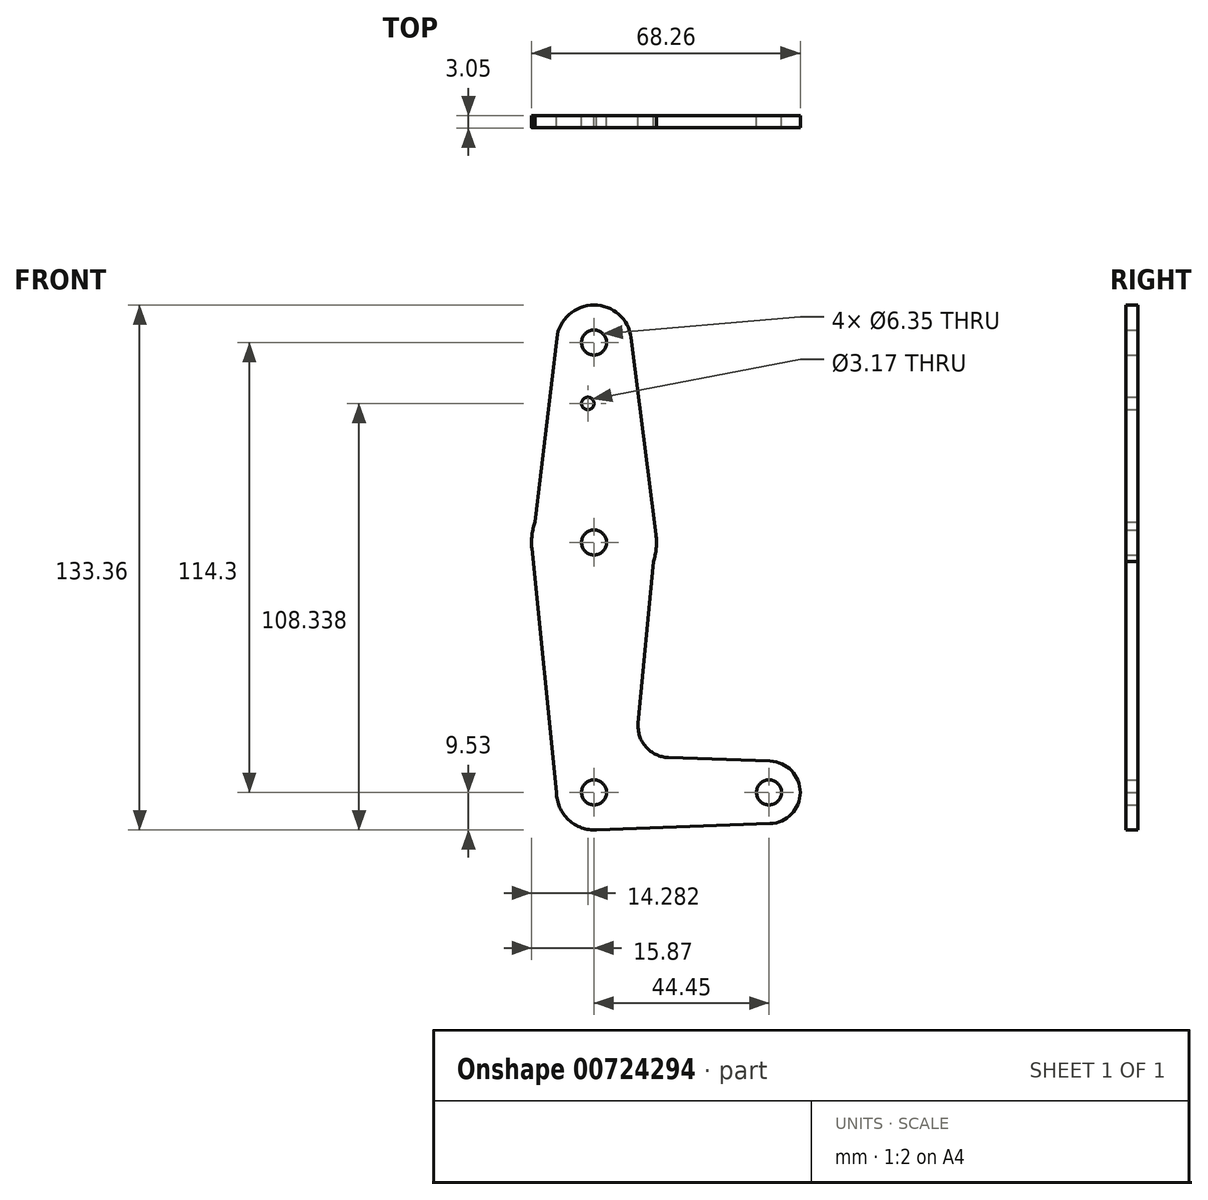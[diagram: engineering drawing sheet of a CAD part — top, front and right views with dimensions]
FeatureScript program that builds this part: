
annotation { "Feature Type Name" : "Feature", "Feature Type Description" : "" }
export const myFeature = defineFeature(function(context is Context, id is Id, definition is map)
    precondition{}
    {
        {
            var Q0;
            Q0=qCreatedBy(makeId("Front.planeOp"),FACE);
            var sketch = newSketch(context, id + "F0", { "sketchPlane" : qUnion([Q0])});
            skLineSegment(sketch, "E0", {"start": v(0, 114.3) * mm, "end": v(0, 0) * mm, "construction": true});
            skLineSegment(sketch, "E1", {"start": v(0, 0) * mm, "end": v(44.45, 0) * mm, "construction": true});
            skCircle(sketch, "E2", {"center": v(0, 114.3) * mm, "radius": 9.53 * mm});
            skCircle(sketch, "E3", {"center": v(0, 0) * mm, "radius": 9.53 * mm});
            skCircle(sketch, "E4", {"center": v(44.45, 0) * mm, "radius": 7.94 * mm});
            skCircle(sketch, "E5", {"center": v(0, 63.5) * mm, "radius": 15.88 * mm});
            skLineSegment(sketch, "E6", {"start": v(-9.52, 0) * mm, "end": v(-15.8, 61.9) * mm});
            skLineSegment(sketch, "E7", {"start": v(-15.8, 61.9) * mm, "end": v(-9.46, 115.42) * mm});
            skLineSegment(sketch, "E8", {"start": v(15.75, 65.48) * mm, "end": v(9.45, 115.5) * mm});
            skLineSegment(sketch, "E9", {"start": v(37.7, 4.2) * mm, "end": v(37.7, 4.2) * mm});
            skLineSegment(sketch, "E10", {"start": v(0, -9.53) * mm, "end": v(44.73, -7.93) * mm});
            skCircle(sketch, "E11", {"center": v(0, 114.3) * mm, "radius": 3.18 * mm});
            skCircle(sketch, "E12", {"center": v(-1.59, 98.8) * mm, "radius": 1.59 * mm});
            skCircle(sketch, "E13", {"center": v(0, 63.5) * mm, "radius": 3.18 * mm});
            skCircle(sketch, "E14", {"center": v(0, 0) * mm, "radius": 3.18 * mm});
            skCircle(sketch, "E15", {"center": v(44.45, 0) * mm, "radius": 3.18 * mm});
            skLineSegment(sketch, "E16", {"start": v(18.86, 8.85) * mm, "end": v(44.73, 7.93) * mm});
            skLineSegment(sketch, "E17", {"start": v(15.75, 65.48) * mm, "end": v(11.22, 17.55) * mm});
            skPoint(sketch, "E18.newPointA", {"position": v(9.57, 0) * mm});
            skPoint(sketch, "E18.newPointB", {"position": v(0, 9.53) * mm});
            skArc(sketch, "E18.filletArc", {"start": v(11.22, 17.55) * mm, "mid": v(13.16, 11.55) * mm, "end": v(18.86, 8.85) * mm});
            skSolve(sketch);
        }
        {
            var Q0;
            Q0 = qSketchRegion(id + "F0", true);
            extrude(context, id + "F1", {"entities" : qUnion([Q0]), "depth" : 3.05 * mm, "offsetDistance" : 25.4 * mm});
        }
    });
